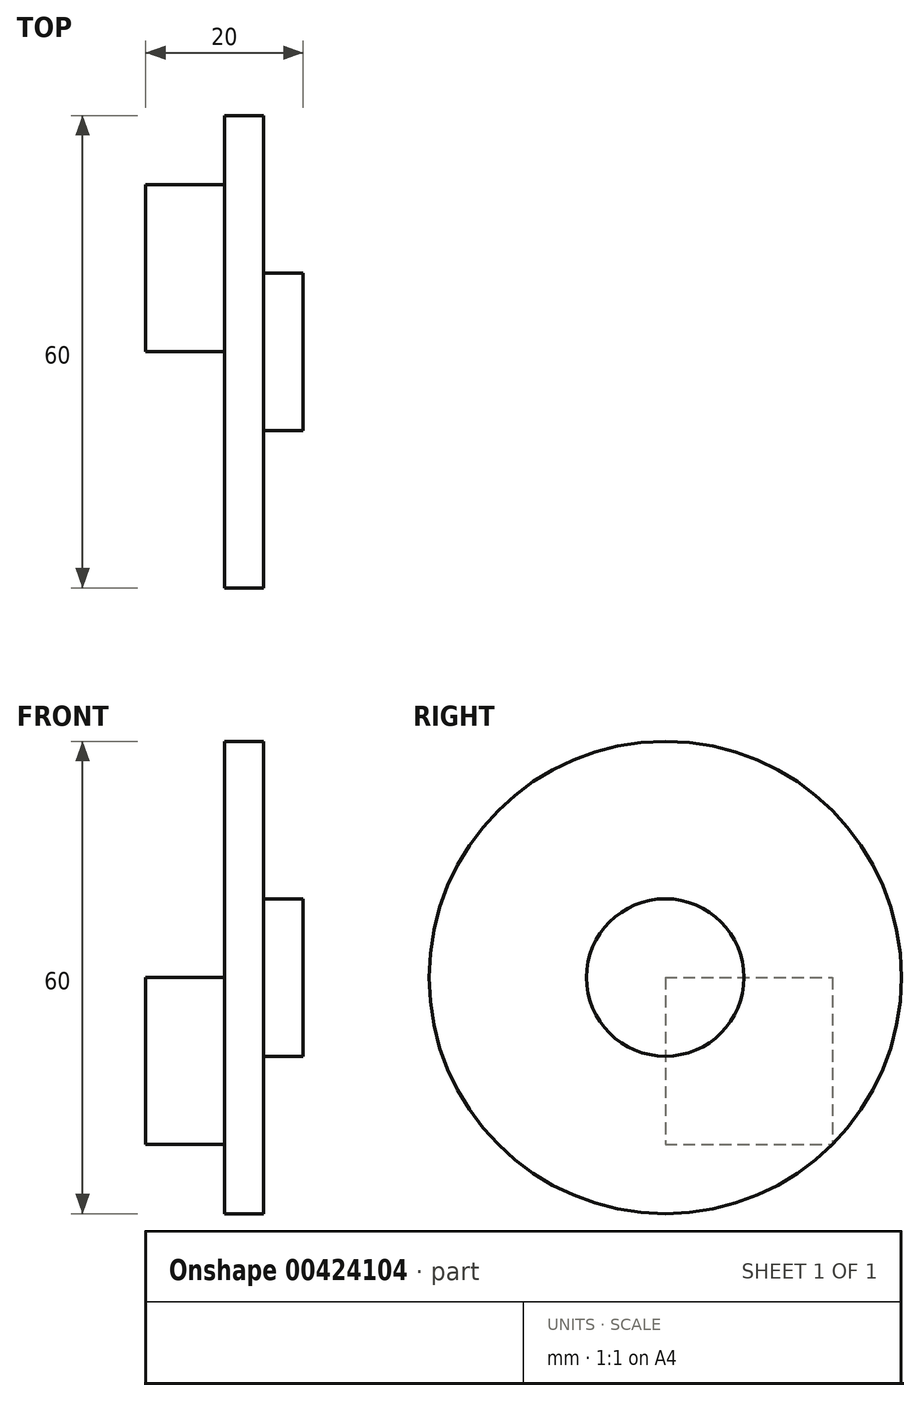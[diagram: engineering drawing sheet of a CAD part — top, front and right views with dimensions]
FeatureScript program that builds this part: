
annotation { "Feature Type Name" : "Feature", "Feature Type Description" : "" }
export const myFeature = defineFeature(function(context is Context, id is Id, definition is map)
    precondition{}
    {
        {
            var Q0;
            Q0=qCreatedBy(makeId("Right.planeOp"),FACE);
            var sketch = newSketch(context, id + "F0", { "sketchPlane" : qUnion([Q0])});
            skCircle(sketch, "E0", {"center": v(0, 0) * mm, "radius": 10 * mm});
            skCircle(sketch, "E1", {"center": v(0, 0) * mm, "radius": 30 * mm});
            skSolve(sketch);
        }
        {
            var Q0;
            Q0=qSketchRegion(id+"F0",true);
            var Q1;
            Q1=makeQuery(id+"F0.imprint","IMPRINT",FACE,{"disambiguationData":[TD([[makeQuery(id+"F0.imprint","IMPRINT",EDGE,{"derivedFrom":sQuery(id+"F0.wireOp",EDGE,"E0")}),1.0]])]});
            extrude(context, id + "F1", {"entities" : qUnion([Q0, Q1]), "oppositeDirection" : true, "depth" : 5 * mm});
        }
        {
            var Q0;
            Q0=makeQuery(id+"F0.imprint","IMPRINT",FACE,{"disambiguationData":[TD([[makeQuery(id+"F0.imprint","IMPRINT",EDGE,{"derivedFrom":sQuery(id+"F0.wireOp",EDGE,"E0")}),1.0]])]});
            extrude(context, id + "F2", {"entities" : qUnion([Q0]), "operationType" : NewBodyOperationType.ADD, "depth" : 5 * mm});
        }
        {
            var Q0;
            Q0=makeQuery(id+"F1.opExtrude","CAP_FACE",FACE,{"disambiguationData":[OSD([sQuery(id+"F0.wireOp",EDGE,"E1")])],"isStart":false});
            var sketch = newSketch(context, id + "F3", { "sketchPlane" : qUnion([Q0])});
            skPoint(sketch, "E2.middle", {"position": v(0, 0) * mm});
            skLineSegment(sketch, "E3.bottom", {"start": v(0, 0) * mm, "end": v(-21.21, 0) * mm});
            skLineSegment(sketch, "E3.top", {"start": v(0, -21.21) * mm, "end": v(-21.21, -21.21) * mm});
            skLineSegment(sketch, "E3.left", {"start": v(0, 0) * mm, "end": v(0, -21.21) * mm});
            skLineSegment(sketch, "E3.right", {"start": v(-21.21, 0) * mm, "end": v(-21.21, -21.21) * mm});
            skSolve(sketch);
        }
        {
            var Q0;
            Q0=makeQuery(id+"F3.imprint","IMPRINT",FACE,{"disambiguationData":[TD([[makeQuery(id+"F3.imprint","IMPRINT",EDGE,{"derivedFrom":sQuery(id+"F3.wireOp",EDGE,"E3.bottom")}),1.0]])]});
            extrude(context, id + "F4", {"entities" : qUnion([Q0]), "operationType" : NewBodyOperationType.ADD, "depth" : 10 * mm});
        }
    });
